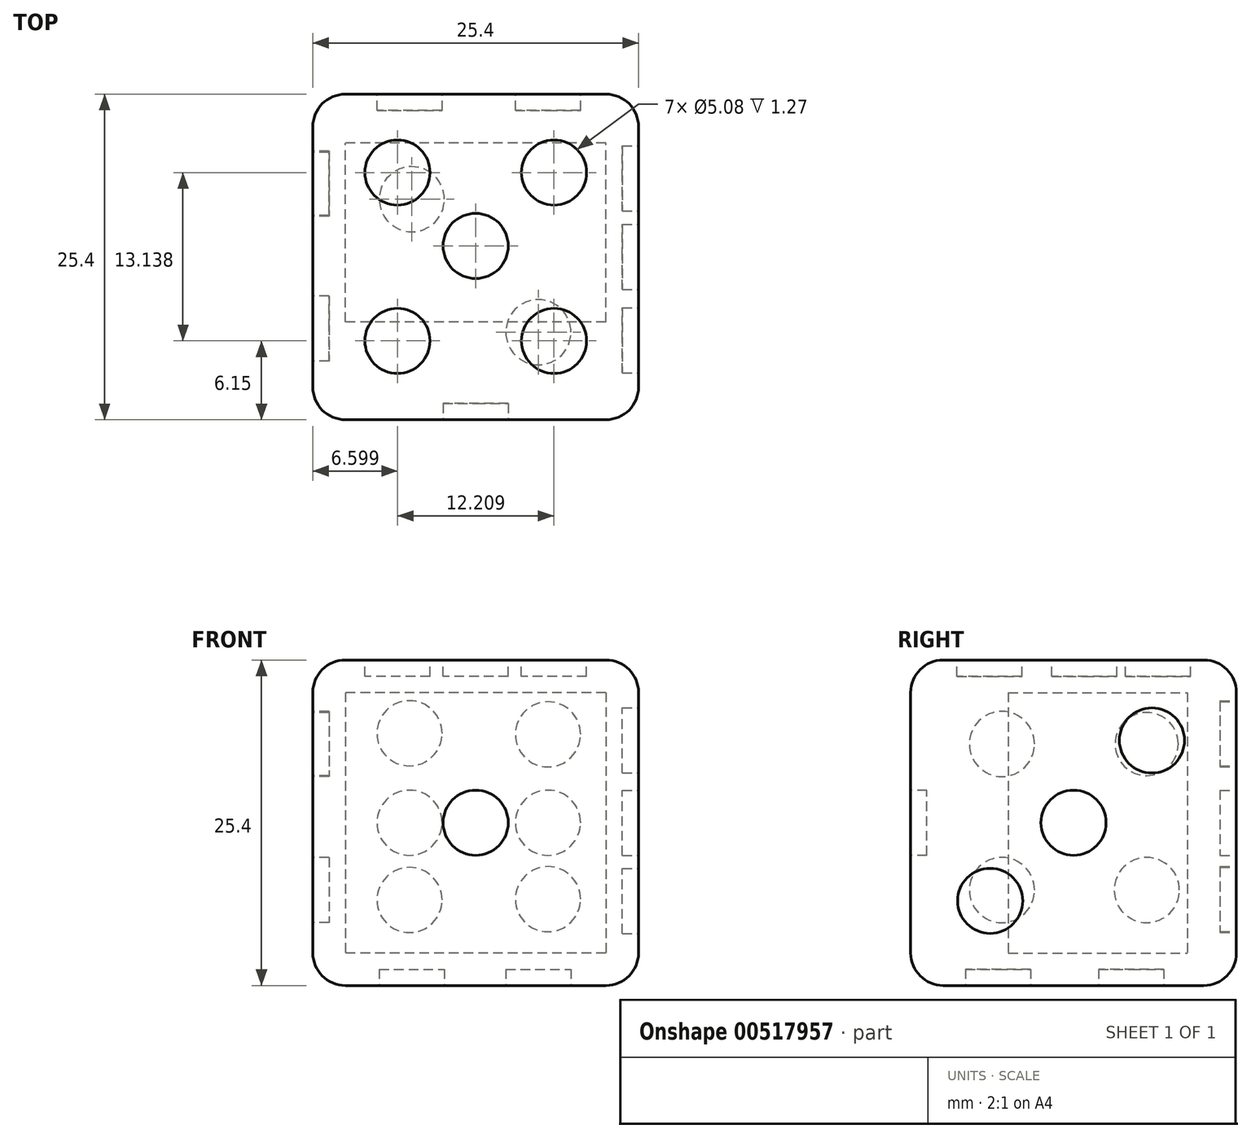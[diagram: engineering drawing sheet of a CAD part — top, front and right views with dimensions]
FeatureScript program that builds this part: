
annotation { "Feature Type Name" : "Feature", "Feature Type Description" : "" }
export const myFeature = defineFeature(function(context is Context, id is Id, definition is map)
    precondition{}
    {
        {
            var Q0;
            Q0=qCreatedBy(makeId("Front.planeOp"),FACE);
            var sketch = newSketch(context, id + "F0", { "sketchPlane" : qUnion([Q0])});
            skLineSegment(sketch, "E0.bottom", {"start": v(12.7, 12.7) * mm, "end": v(-12.7, 12.7) * mm});
            skLineSegment(sketch, "E0.top", {"start": v(12.7, -12.7) * mm, "end": v(-12.7, -12.7) * mm});
            skLineSegment(sketch, "E0.left", {"start": v(12.7, 12.7) * mm, "end": v(12.7, -12.7) * mm});
            skLineSegment(sketch, "E0.right", {"start": v(-12.7, 12.7) * mm, "end": v(-12.7, -12.7) * mm});
            skPoint(sketch, "E0.middle", {"position": v(0, 0) * mm});
            skSolve(sketch);
        }
        {
            var Q0;
            Q0 = qSketchRegion(id + "F0", true);
            extrude(context, id + "F1", {"entities" : qUnion([Q0]), "depth" : 25.4 * mm, "offsetDistance" : 25.4 * mm});
        }
        {
            var Q0;
            Q0=makeQuery(id+"F1.opExtrude","SWEPT_EDGE",EDGE,{"disambiguationData":[OSD([sQuery(id+"F0.wireOp",EDGE,"E0.bottom"),sQuery(id+"F0.wireOp",EDGE,"E0.left")])]});
            var Q1;
            Q1=makeQuery(id+"F1.opExtrude","CAP_EDGE",EDGE,{"disambiguationData":[OSD([sQuery(id+"F0.wireOp",EDGE,"E0.left")])],"isStart":false});
            var Q2;
            Q2=makeQuery(id+"F1.opExtrude","SWEPT_EDGE",EDGE,{"disambiguationData":[OSD([sQuery(id+"F0.wireOp",EDGE,"E0.top"),sQuery(id+"F0.wireOp",EDGE,"E0.left")])]});
            var Q3;
            Q3=makeQuery(id+"F1.opExtrude","CAP_EDGE",EDGE,{"disambiguationData":[OSD([sQuery(id+"F0.wireOp",EDGE,"E0.left")])],"isStart":true});
            var Q4;
            Q4=makeQuery(id+"F1.opExtrude","CAP_EDGE",EDGE,{"disambiguationData":[OSD([sQuery(id+"F0.wireOp",EDGE,"E0.bottom")])],"isStart":true});
            var Q5;
            Q5=makeQuery(id+"F1.opExtrude","CAP_EDGE",EDGE,{"disambiguationData":[OSD([sQuery(id+"F0.wireOp",EDGE,"E0.top")])],"isStart":true});
            var Q6;
            Q6=makeQuery(id+"F1.opExtrude","CAP_EDGE",EDGE,{"disambiguationData":[OSD([sQuery(id+"F0.wireOp",EDGE,"E0.top")])],"isStart":false});
            var Q7;
            Q7=makeQuery(id+"F1.opExtrude","CAP_EDGE",EDGE,{"disambiguationData":[OSD([sQuery(id+"F0.wireOp",EDGE,"E0.bottom")])],"isStart":false});
            var Q8;
            Q8=makeQuery(id+"F1.opExtrude","CAP_EDGE",EDGE,{"disambiguationData":[OSD([sQuery(id+"F0.wireOp",EDGE,"E0.right")])],"isStart":false});
            var Q9;
            Q9=makeQuery(id+"F1.opExtrude","SWEPT_EDGE",EDGE,{"disambiguationData":[OSD([sQuery(id+"F0.wireOp",EDGE,"E0.bottom"),sQuery(id+"F0.wireOp",EDGE,"E0.right")])]});
            var Q10;
            Q10=makeQuery(id+"F1.opExtrude","CAP_EDGE",EDGE,{"disambiguationData":[OSD([sQuery(id+"F0.wireOp",EDGE,"E0.right")])],"isStart":true});
            var Q11;
            Q11=makeQuery(id+"F1.opExtrude","SWEPT_EDGE",EDGE,{"disambiguationData":[OSD([sQuery(id+"F0.wireOp",EDGE,"E0.top"),sQuery(id+"F0.wireOp",EDGE,"E0.right")])]});
            fillet(context, id + "F2", {"entities" : qUnion([Q0, Q1, Q2, Q3, Q4, Q5, Q6, Q7, Q8, Q9, Q10, Q11]), "radius" : 2.54 * mm, "tangentPropagation" : true, "allowEdgeOverflow" : false});
        }
        {
            var Q0;
            Q0=makeQuery(id+"F1.opExtrude","CAP_FACE",FACE,{"disambiguationData":[OSD([sQuery(id+"F0.wireOp",EDGE,"E0.bottom"),sQuery(id+"F0.wireOp",EDGE,"E0.top"),sQuery(id+"F0.wireOp",EDGE,"E0.left"),sQuery(id+"F0.wireOp",EDGE,"E0.right")])],"isStart":true});
            extrude(context, id + "F3", {"entities" : qUnion([Q0]), "operationType" : NewBodyOperationType.REMOVE, "oppositeDirection" : true, "depth" : 17.78 * mm, "offsetDistance" : 25.4 * mm});
        }
        {
            var Q0;
            Q0=qCreatedBy(makeId("Front.planeOp"),FACE);
            var sketch = newSketch(context, id + "F4", { "sketchPlane" : qUnion([Q0])});
            skLineSegment(sketch, "E1.bottom", {"start": v(10.16, 10.16) * mm, "end": v(-10.16, 10.16) * mm});
            skLineSegment(sketch, "E1.top", {"start": v(10.16, -10.16) * mm, "end": v(-10.16, -10.16) * mm});
            skLineSegment(sketch, "E1.left", {"start": v(10.16, 10.16) * mm, "end": v(10.16, -10.16) * mm});
            skLineSegment(sketch, "E1.right", {"start": v(-10.16, 10.16) * mm, "end": v(-10.16, -10.16) * mm});
            skPoint(sketch, "E1.middle", {"position": v(0, 0) * mm});
            skSolve(sketch);
        }
        {
            var Q0;
            Q0 = qSketchRegion(id + "F4", true);
            extrude(context, id + "F5", {"entities" : qUnion([Q0]), "operationType" : NewBodyOperationType.ADD, "depth" : 3.8 * mm, "offsetDistance" : 25.4 * mm});
        }
        {
            var Q0;
            Q0=makeQuery(id+"F5.opExtrude","CAP_FACE",FACE,{"disambiguationData":[OSD([sQuery(id+"F4.wireOp",EDGE,"E1.bottom"),sQuery(id+"F4.wireOp",EDGE,"E1.top"),sQuery(id+"F4.wireOp",EDGE,"E1.left"),sQuery(id+"F4.wireOp",EDGE,"E1.right")])],"isStart":true});
            var sketch = newSketch(context, id + "F6", { "sketchPlane" : qUnion([Q0])});
            skCircle(sketch, "E2", {"center": v(-5.63, 0) * mm, "radius": 2.54 * mm});
            skCircle(sketch, "E3", {"center": v(-5.63, 6.9) * mm, "radius": 2.54 * mm});
            skCircle(sketch, "E4", {"center": v(-5.63, -5.96) * mm, "radius": 2.54 * mm});
            skCircle(sketch, "E5", {"center": v(5.16, 0) * mm, "radius": 2.54 * mm});
            skCircle(sketch, "E6", {"center": v(5.16, 6.98) * mm, "radius": 2.54 * mm});
            skCircle(sketch, "E7", {"center": v(5.16, -6.03) * mm, "radius": 2.54 * mm});
            skSolve(sketch);
        }
        {
            var Q0;
            Q0 = qSketchRegion(id + "F6", true);
            extrude(context, id + "F7", {"entities" : qUnion([Q0]), "operationType" : NewBodyOperationType.REMOVE, "oppositeDirection" : true, "depth" : 1.27 * mm, "offsetDistance" : 25.4 * mm});
        }
        {
            var Q0;
            Q0=makeQuery(id+"F1.opExtrude","CAP_FACE",FACE,{"disambiguationData":[OSD([sQuery(id+"F0.wireOp",EDGE,"E0.bottom"),sQuery(id+"F0.wireOp",EDGE,"E0.top"),sQuery(id+"F0.wireOp",EDGE,"E0.left"),sQuery(id+"F0.wireOp",EDGE,"E0.right")])],"isStart":false});
            var sketch = newSketch(context, id + "F8", { "sketchPlane" : qUnion([Q0])});
            skCircle(sketch, "E8", {"center": v(0, 0) * mm, "radius": 2.54 * mm});
            skSolve(sketch);
        }
        {
            var Q0;
            Q0 = qSketchRegion(id + "F8", true);
            extrude(context, id + "F9", {"entities" : qUnion([Q0]), "operationType" : NewBodyOperationType.REMOVE, "oppositeDirection" : true, "depth" : 1.27 * mm, "offsetDistance" : 25.4 * mm});
        }
        {
            var Q0;
            Q0=makeQuery(id+"F1.opExtrude","SWEPT_FACE",FACE,{"disambiguationData":[OSD([sQuery(id+"F0.wireOp",EDGE,"E0.left")])]});
            var sketch = newSketch(context, id + "F10", { "sketchPlane" : qUnion([Q0])});
            skCircle(sketch, "E9", {"center": v(-12.7, 0) * mm, "radius": 2.54 * mm});
            skPoint(sketch, "E9.centerSnap0", {"position": v(-12.7, -10.16) * mm});
            skCircle(sketch, "E10", {"center": v(-6.58, 6.42) * mm, "radius": 2.54 * mm});
            skCircle(sketch, "E11", {"center": v(-19.2, -6.1) * mm, "radius": 2.54 * mm});
            skSolve(sketch);
        }
        {
            var Q0;
            Q0 = qSketchRegion(id + "F10", true);
            var Q1;
            Q1=makeQuery(id+"F1.opExtrude","SWEPT_FACE",FACE,{"disambiguationData":[OSD([sQuery(id+"F0.wireOp",EDGE,"E0.right")])]});
            extrude(context, id + "F11", {"entities" : qUnion([Q0, Q1]), "operationType" : NewBodyOperationType.REMOVE, "oppositeDirection" : true, "depth" : 1.27 * mm, "offsetDistance" : 25.4 * mm});
        }
        {
            var Q0;
            Q0=makeQuery(id+"F1.opExtrude","SWEPT_FACE",FACE,{"disambiguationData":[OSD([sQuery(id+"F0.wireOp",EDGE,"E0.right")])]});
            var sketch = newSketch(context, id + "F12", { "sketchPlane" : qUnion([Q0])});
            skCircle(sketch, "E12", {"center": v(6.99, 6.14) * mm, "radius": 2.46 * mm});
            skCircle(sketch, "E13", {"center": v(6.99, -5.25) * mm, "radius": 2.54 * mm});
            skCircle(sketch, "E14", {"center": v(18.28, 6.14) * mm, "radius": 2.54 * mm});
            skCircle(sketch, "E15", {"center": v(18.28, -5.25) * mm, "radius": 2.54 * mm});
            skSolve(sketch);
        }
        {
            var Q0;
            Q0 = qSketchRegion(id + "F12", true);
            extrude(context, id + "F13", {"entities" : qUnion([Q0]), "operationType" : NewBodyOperationType.REMOVE, "oppositeDirection" : true, "depth" : 1.27 * mm, "offsetDistance" : 25.4 * mm});
        }
        {
            var Q0;
            Q0=makeQuery(id+"F1.opExtrude","SWEPT_FACE",FACE,{"disambiguationData":[OSD([sQuery(id+"F0.wireOp",EDGE,"E0.top")])]});
            var sketch = newSketch(context, id + "F14", { "sketchPlane" : qUnion([Q0])});
            skCircle(sketch, "E16", {"center": v(4.89, 18.57) * mm, "radius": 2.54 * mm});
            skCircle(sketch, "E17", {"center": v(-4.98, 8.2) * mm, "radius": 2.54 * mm});
            skSolve(sketch);
        }
        {
            var Q0;
            Q0 = qSketchRegion(id + "F14", true);
            extrude(context, id + "F15", {"entities" : qUnion([Q0]), "operationType" : NewBodyOperationType.REMOVE, "oppositeDirection" : true, "depth" : 1.27 * mm, "offsetDistance" : 25.4 * mm});
        }
        {
            var Q0;
            Q0=makeQuery(id+"F1.opExtrude","SWEPT_FACE",FACE,{"disambiguationData":[OSD([sQuery(id+"F0.wireOp",EDGE,"E0.bottom")])]});
            var sketch = newSketch(context, id + "F16", { "sketchPlane" : qUnion([Q0])});
            skCircle(sketch, "E18", {"center": v(0, -11.84) * mm, "radius": 2.54 * mm});
            skCircle(sketch, "E19", {"center": v(-6.1, -6.11) * mm, "radius": 2.54 * mm});
            skCircle(sketch, "E20", {"center": v(6.1, -6.11) * mm, "radius": 2.54 * mm});
            skCircle(sketch, "E21", {"center": v(-6.1, -19.25) * mm, "radius": 2.54 * mm});
            skCircle(sketch, "E22", {"center": v(6.1, -19.25) * mm, "radius": 2.54 * mm});
            skSolve(sketch);
        }
        {
            var Q0;
            Q0 = qSketchRegion(id + "F16", true);
            extrude(context, id + "F17", {"entities" : qUnion([Q0]), "operationType" : NewBodyOperationType.REMOVE, "oppositeDirection" : true, "depth" : 1.27 * mm, "offsetDistance" : 25.4 * mm});
        }
    });
